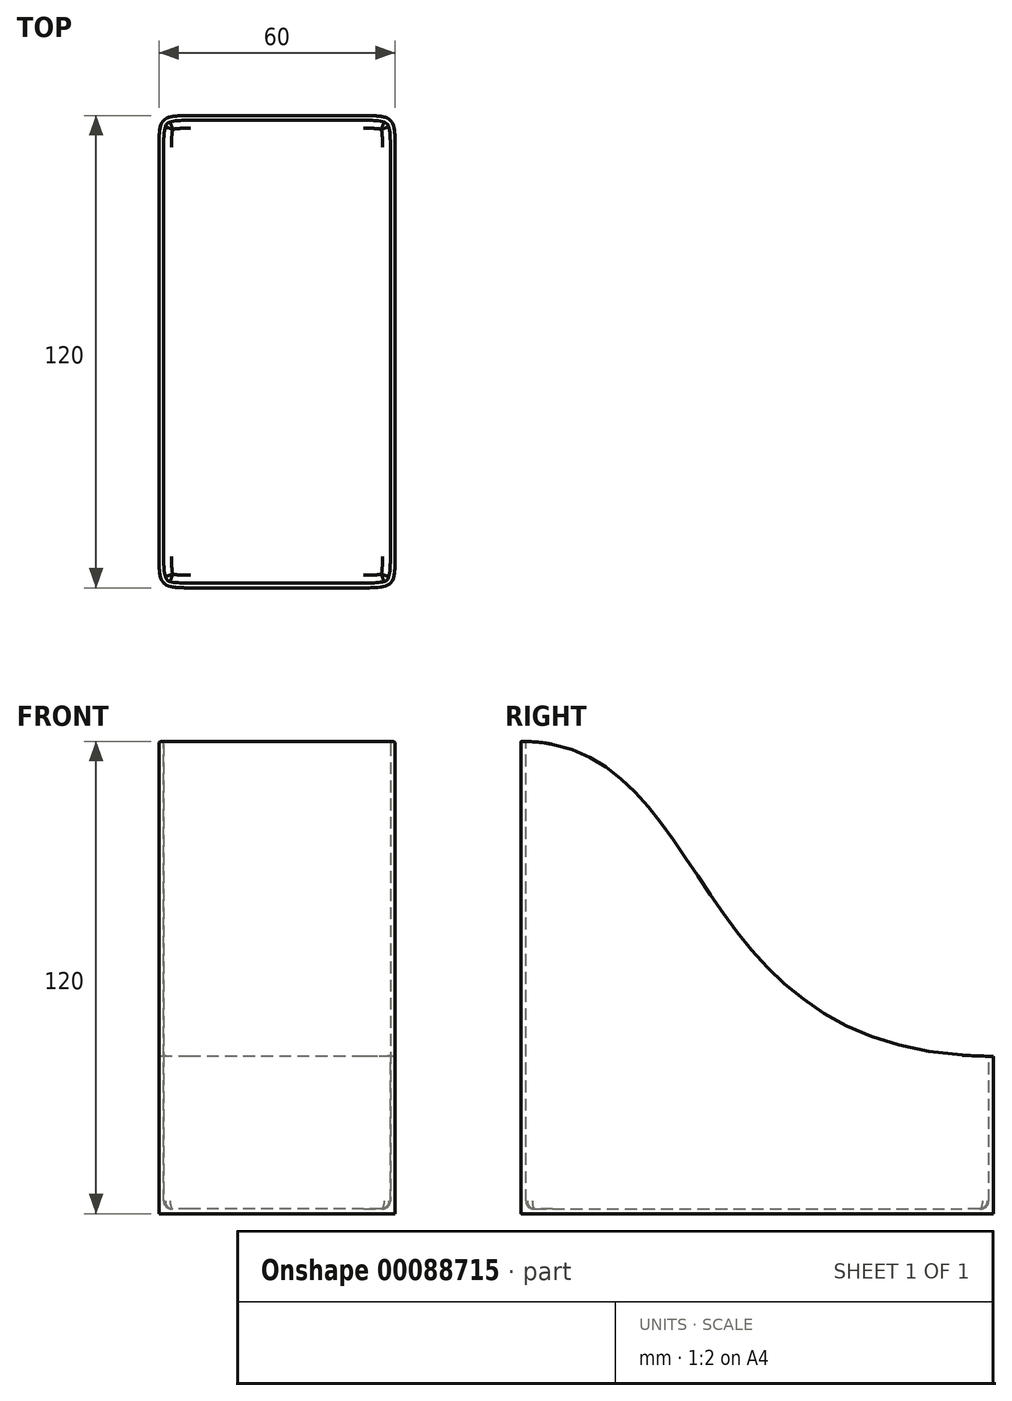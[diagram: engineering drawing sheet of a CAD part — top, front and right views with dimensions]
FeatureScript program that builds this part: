
annotation { "Feature Type Name" : "Feature", "Feature Type Description" : "" }
export const myFeature = defineFeature(function(context is Context, id is Id, definition is map)
    precondition{}
    {
        {
            var Q0;
            Q0=qCreatedBy(makeId("Right.planeOp"),FACE);
            var sketch = newSketch(context, id + "F0", { "sketchPlane" : qUnion([Q0])});
            skLineSegment(sketch, "E0", {"start": v(0, 0) * mm, "end": v(120, 0) * mm});
            skLineSegment(sketch, "E1", {"start": v(120, 0) * mm, "end": v(120, 40) * mm});
            skLineSegment(sketch, "E2", {"start": v(0, 120) * mm, "end": v(0, 0) * mm});
            skFitSpline(sketch, "E3", {"points": [v(0, 120) * mm, v(120, 40) * mm], "startDerivative": vector(150, 0) * mm, "endDerivative": vector(240, 0) * mm});
            skLineSegment(sketch, "E4", {"start": v(50, 120) * mm, "end": v(40, 40) * mm, "construction": true});
            skSolve(sketch);
        }
        {
            var Q0;
            Q0 = qSketchRegion(id + "F0", true);
            extrude(context, id + "F1", {"entities" : qUnion([Q0]), "depth" : 60 * mm, "symmetric" : true});
        }
        {
            var Q0;
            Q0=makeQuery(id+"F1.opExtrude","CAP_EDGE",EDGE,{"disambiguationData":[OSD([sQuery(id+"F0.wireOp",EDGE,"E2")])],"isStart":false});
            var Q1;
            Q1=makeQuery(id+"F1.opExtrude","CAP_EDGE",EDGE,{"disambiguationData":[OSD([sQuery(id+"F0.wireOp",EDGE,"E1")])],"isStart":false});
            var Q2;
            Q2=makeQuery(id+"F1.opExtrude","CAP_EDGE",EDGE,{"disambiguationData":[OSD([sQuery(id+"F0.wireOp",EDGE,"E1")])],"isStart":true});
            var Q3;
            Q3=makeQuery(id+"F1.opExtrude","CAP_EDGE",EDGE,{"disambiguationData":[OSD([sQuery(id+"F0.wireOp",EDGE,"E2")])],"isStart":true});
            fillet(context, id + "F2", {"entities" : qUnion([Q0, Q1, Q2, Q3]), "radius" : 8 * mm, "tangentPropagation" : true, "rho" : .7, "crossSection" : FilletCrossSection.CONIC, "allowEdgeOverflow" : false});
        }
        {
            var Q0;
            Q0=makeQuery(id+"F1.opExtrude","SWEPT_FACE",FACE,{"disambiguationData":[OSD([sQuery(id+"F0.wireOp",EDGE,"E3")])]});
            shell(context, id + "F3", {"entities" : qUnion([Q0]), "thickness" : 1.2 * mm});
        }
        {
            var Q0;
            Q0=makeQuery(id+"F3.opShell","OFFSET_FACE",FACE,{"disambiguationData":[OSD([sQuery(id+"F0.wireOp",EDGE,"E0")])]});
            fillet(context, id + "F4", {"entities" : qUnion([Q0]), "radius" : 2 * mm, "tangentPropagation" : true, "allowEdgeOverflow" : false});
        }
    });
